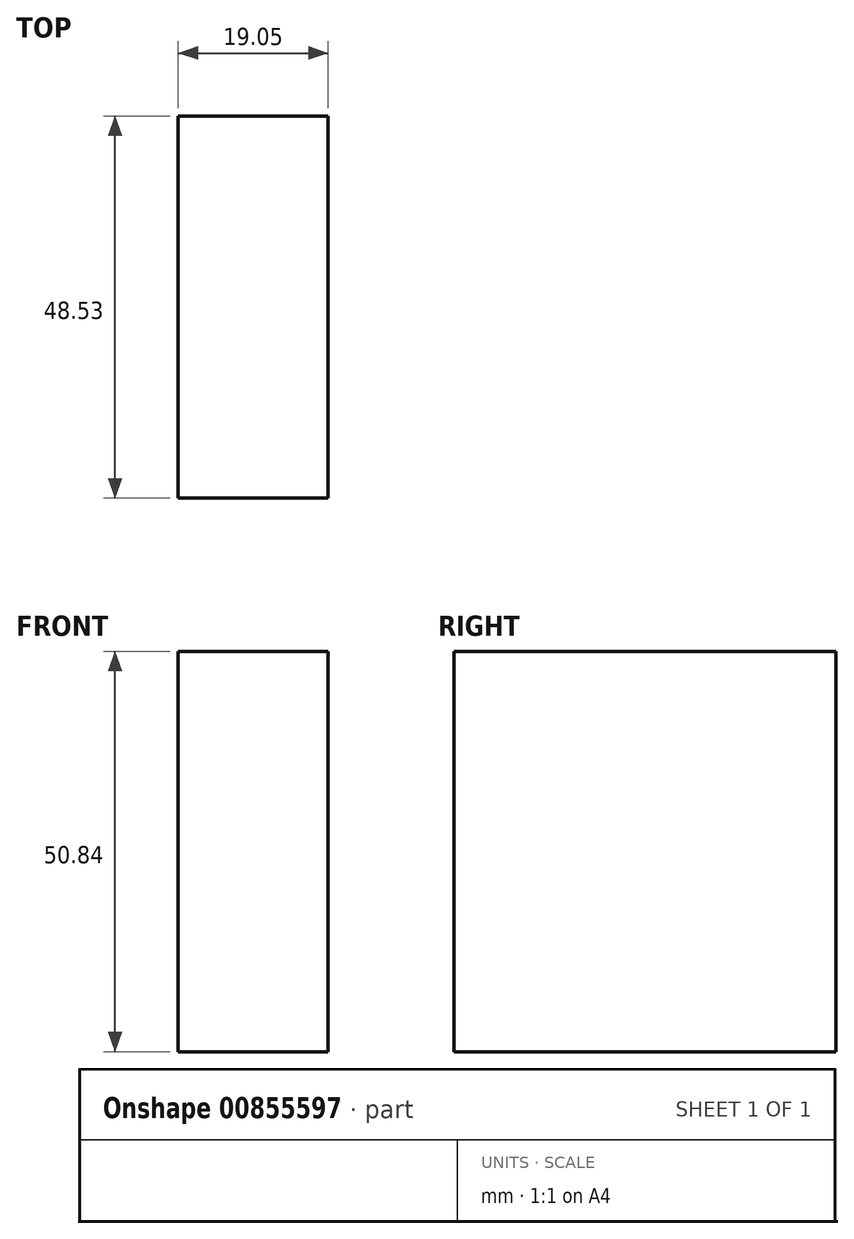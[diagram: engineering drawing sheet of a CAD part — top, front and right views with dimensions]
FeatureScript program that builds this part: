
annotation { "Feature Type Name" : "Feature", "Feature Type Description" : "" }
export const myFeature = defineFeature(function(context is Context, id is Id, definition is map)
    precondition{}
    {
        {
            var Q0;
            Q0=qCreatedBy(makeId("Right.planeOp"),FACE);
            var sketch = newSketch(context, id + "F0", { "sketchPlane" : qUnion([Q0])});
            skLineSegment(sketch, "E0.bottom", {"start": v(0, 0) * mm, "end": v(48.53, 0) * mm});
            skLineSegment(sketch, "E0.top", {"start": v(0, 50.84) * mm, "end": v(48.53, 50.84) * mm});
            skLineSegment(sketch, "E0.left", {"start": v(0, 0) * mm, "end": v(0, 50.84) * mm});
            skLineSegment(sketch, "E0.right", {"start": v(48.53, 0) * mm, "end": v(48.53, 50.84) * mm});
            skSolve(sketch);
        }
        {
            var Q0;
            Q0 = qSketchRegion(id + "F0", true);
            extrude(context, id + "F1", {"entities" : qUnion([Q0]), "depth" : 19.05 * mm, "offsetDistance" : 25.4 * mm});
        }
    });
